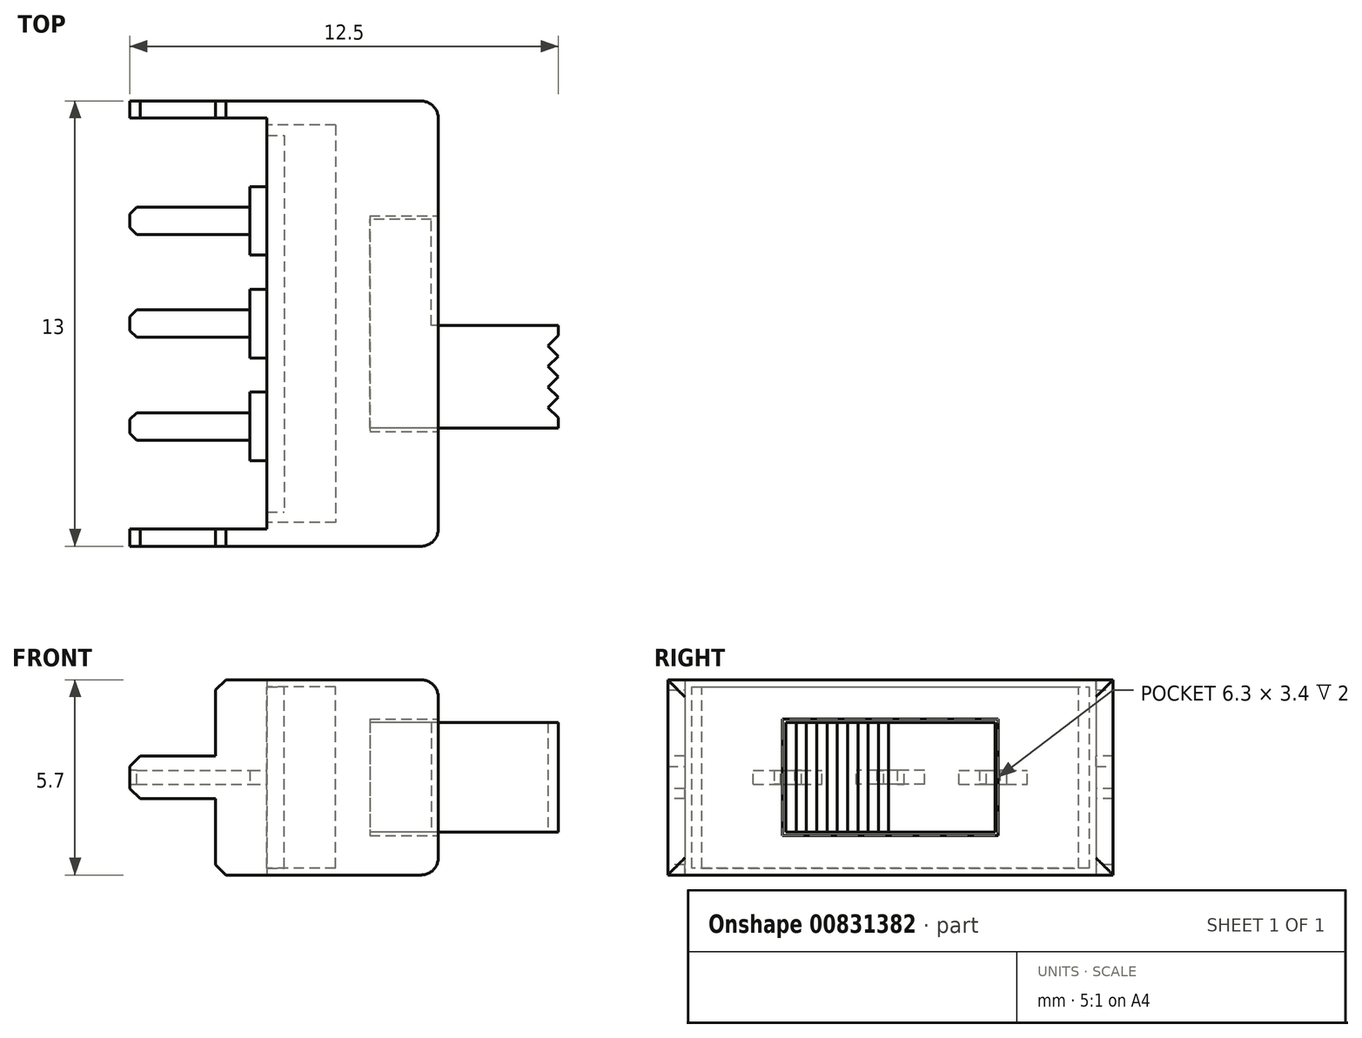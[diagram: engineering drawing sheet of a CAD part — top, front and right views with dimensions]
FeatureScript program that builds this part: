
annotation { "Feature Type Name" : "Feature", "Feature Type Description" : "" }
export const myFeature = defineFeature(function(context is Context, id is Id, definition is map)
    precondition{}
    {
        {
            var Q0;
            Q0=qCreatedBy(makeId("Top.planeOp"),FACE);
            var sketch = newSketch(context, id + "F0", { "sketchPlane" : qUnion([Q0])});
            skLineSegment(sketch, "E0.bottom", {"start": v(2.5, 6.5) * mm, "end": v(-2.5, 6.5) * mm});
            skLineSegment(sketch, "E0.top", {"start": v(2.5, -6.5) * mm, "end": v(-2.5, -6.5) * mm});
            skLineSegment(sketch, "E0.left", {"start": v(2.5, 6.5) * mm, "end": v(2.5, -6.5) * mm});
            skLineSegment(sketch, "E0.right", {"start": v(-2.5, 6.5) * mm, "end": v(-2.5, -6.5) * mm});
            skPoint(sketch, "E0.middle", {"position": v(0, 0) * mm});
            skSolve(sketch);
        }
        {
            var Q0;
            Q0=qSketchRegion(id+"F0",true);
            extrude(context, id + "F1", {"entities" : qUnion([Q0]), "depth" : 5.7 * mm, "offsetDistance" : 25 * mm});
        }
        {
            var Q0;
            Q0=makeQuery(id+"F1.opExtrude","SWEPT_FACE",FACE,{"disambiguationData":[OSD([sQuery(id+"F0.wireOp",EDGE,"E0.left")])]});
            var sketch = newSketch(context, id + "F2", { "sketchPlane" : qUnion([Q0])});
            skLineSegment(sketch, "E1.bottom", {"start": v(3.15, 4.55) * mm, "end": v(-3.15, 4.55) * mm});
            skLineSegment(sketch, "E1.top", {"start": v(3.15, 1.15) * mm, "end": v(-3.15, 1.15) * mm});
            skLineSegment(sketch, "E1.left", {"start": v(3.15, 4.55) * mm, "end": v(3.15, 1.15) * mm});
            skLineSegment(sketch, "E1.right", {"start": v(-3.15, 4.55) * mm, "end": v(-3.15, 1.15) * mm});
            skPoint(sketch, "E1.middle", {"position": v(0, 2.85) * mm});
            skPoint(sketch, "E1.middle.positionSnap0", {"position": v(-6.5, 2.85) * mm});
            skPoint(sketch, "E1.middle.positionSnap1", {"position": v(0, 5.7) * mm});
            skPoint(sketch, "E1.centerSnap0", {"position": v(-6.5, 2.85) * mm});
            skPoint(sketch, "E1.centerSnap1", {"position": v(0, 5.7) * mm});
            skSolve(sketch);
        }
        {
            var Q0;
            Q0=qSketchRegion(id+"F2",true);
            extrude(context, id + "F3", {"entities" : qUnion([Q0]), "operationType" : NewBodyOperationType.REMOVE, "oppositeDirection" : true, "depth" : 2 * mm, "offsetDistance" : 25 * mm});
        }
        {
            var Q0;
            Q0=makeQuery(id+"F3.boolean.opBoolean","COPY",FACE,{"derivedFrom":makeQuery(id+"F3.opExtrude","CAP_FACE",FACE,{"disambiguationData":[OSD([sQuery(id+"F2.wireOp",EDGE,"E1.bottom"),sQuery(id+"F2.wireOp",EDGE,"E1.top"),sQuery(id+"F2.wireOp",EDGE,"E1.left"),sQuery(id+"F2.wireOp",EDGE,"E1.right")])],"isStart":false})});
            var sketch = newSketch(context, id + "F4", { "sketchPlane" : qUnion([Q0])});
            skLineSegment(sketch, "E2.0", {"start": v(-3.05, 1.25) * mm, "end": v(3.05, 1.25) * mm});
            skLineSegment(sketch, "E2.1", {"start": v(-3.05, 4.45) * mm, "end": v(-3.05, 1.25) * mm});
            skLineSegment(sketch, "E2.2", {"start": v(3.05, 4.45) * mm, "end": v(-3.05, 4.45) * mm});
            skLineSegment(sketch, "E2.3", {"start": v(3.05, 1.25) * mm, "end": v(3.05, 4.45) * mm});
            skSolve(sketch);
        }
        {
            var Q0;
            Q0=makeQuery(id+"F4.imprint","IMPRINT",FACE,{"disambiguationData":[TD([[makeQuery(id+"F4.imprint","IMPRINT",EDGE,{"derivedFrom":sQuery(id+"F4.wireOp",EDGE,"E2.0")}),1.0]])]});
            extrude(context, id + "F5", {"entities" : qUnion([Q0]), "depth" : 1.8 * mm, "offsetDistance" : 25 * mm});
        }
        {
            var Q0;
            Q0=makeQuery(id+"F5.opExtrude","CAP_FACE",FACE,{"disambiguationData":[OSD([sQuery(id+"F4.wireOp",EDGE,"E2.0"),sQuery(id+"F4.wireOp",EDGE,"E2.1"),sQuery(id+"F4.wireOp",EDGE,"E2.2"),sQuery(id+"F4.wireOp",EDGE,"E2.3")])],"isStart":false});
            var sketch = newSketch(context, id + "F6", { "sketchPlane" : qUnion([Q0])});
            skLineSegment(sketch, "E3", {"start": v(-0.05, 4.45) * mm, "end": v(-0.05, 1.25) * mm});
            skSolve(sketch);
        }
        {
            var Q0;
            Q0=qSketchRegion(id+"F6",true);
            var Q1;
            {var subQ0=sQuery(id+"F6.wireOp",EDGE,"E3");Q1=makeQuery(id+"F6.imprint","IMPRINT",FACE,{"disambiguationData":[TD([[makeQuery(id+"F6.imprint","IMPRINT",EDGE,{"derivedFrom":subQ0}),-1.0]])]});}
            extrude(context, id + "F7", {"entities" : qUnion([Q0, Q1]), "operationType" : NewBodyOperationType.ADD, "depth" : 3.7 * mm, "offsetDistance" : 25 * mm});
        }
        {
            var Q0;
            Q0=makeQuery(id+"F1.opExtrude","SWEPT_FACE",FACE,{"disambiguationData":[OSD([sQuery(id+"F0.wireOp",EDGE,"E0.right")])]});
            var sketch = newSketch(context, id + "F8", { "sketchPlane" : qUnion([Q0])});
            skLineSegment(sketch, "E4", {"start": v(-6, 5.7) * mm, "end": v(-6, 0) * mm});
            skLineSegment(sketch, "E5", {"start": v(6, 5.7) * mm, "end": v(6, 0) * mm});
            skSolve(sketch);
        }
        {
            var Q0;
            Q0=qSketchRegion(id+"F8",true);
            var Q1;
            {var subQ0=sQuery(id+"F8.wireOp",EDGE,"E4");Q1=makeQuery(id+"F8.imprint","IMPRINT",FACE,{"disambiguationData":[TD([[makeQuery(id+"F8.imprint","IMPRINT",EDGE,{"derivedFrom":subQ0}),-1.0]])]});}
            var Q2;
            {var subQ0=sQuery(id+"F8.wireOp",EDGE,"E5");Q2=makeQuery(id+"F8.imprint","IMPRINT",FACE,{"disambiguationData":[TD([[makeQuery(id+"F8.imprint","IMPRINT",EDGE,{"derivedFrom":subQ0}),1.0]])]});}
            extrude(context, id + "F9", {"entities" : qUnion([Q0, Q1, Q2]), "operationType" : NewBodyOperationType.ADD, "depth" : 1.5 * mm, "offsetDistance" : 25 * mm});
        }
        {
            var Q0;
            Q0=makeQuery(id+"F1.opExtrude","CAP_EDGE",EDGE,{"disambiguationData":[OSD([sQuery(id+"F0.wireOp",EDGE,"E0.left")])],"isStart":false});
            var Q1;
            Q1=makeQuery(id+"F1.opExtrude","SWEPT_EDGE",EDGE,{"disambiguationData":[OSD([sQuery(id+"F0.wireOp",EDGE,"E0.bottom"),sQuery(id+"F0.wireOp",EDGE,"E0.left")])]});
            var Q2;
            Q2=makeQuery(id+"F1.opExtrude","CAP_EDGE",EDGE,{"disambiguationData":[OSD([sQuery(id+"F0.wireOp",EDGE,"E0.left")])],"isStart":true});
            var Q3;
            Q3=makeQuery(id+"F1.opExtrude","SWEPT_EDGE",EDGE,{"disambiguationData":[OSD([sQuery(id+"F0.wireOp",EDGE,"E0.top"),sQuery(id+"F0.wireOp",EDGE,"E0.left")])]});
            fillet(context, id + "F10", {"entities" : qUnion([Q0, Q1, Q2, Q3]), "radius" : 0.5 * mm, "tangentPropagation" : true, "allowEdgeOverflow" : false});
        }
        {
            var Q0;
            Q0=makeQuery(id+"F1.opExtrude","SWEPT_FACE",FACE,{"disambiguationData":[OSD([sQuery(id+"F0.wireOp",EDGE,"E0.right")])]});
            var sketch = newSketch(context, id + "F11", { "sketchPlane" : qUnion([Q0])});
            skLineSegment(sketch, "E6.0", {"start": v(5.8, 0.2) * mm, "end": v(5.8, 5.5) * mm});
            skLineSegment(sketch, "E6.1", {"start": v(-5.8, 0.2) * mm, "end": v(5.8, 0.2) * mm});
            skLineSegment(sketch, "E6.2", {"start": v(-5.8, 5.5) * mm, "end": v(-5.8, 0.2) * mm});
            skLineSegment(sketch, "E6.3", {"start": v(5.8, 5.5) * mm, "end": v(-5.8, 5.5) * mm});
            skSolve(sketch);
        }
        {
            var Q0;
            Q0=qSketchRegion(id+"F11",true);
            extrude(context, id + "F12", {"entities" : qUnion([Q0]), "operationType" : NewBodyOperationType.REMOVE, "oppositeDirection" : true, "depth" : 2 * mm, "offsetDistance" : 25 * mm});
        }
        {
            var Q0;
            Q0=makeQuery(id+"F12.boolean.opBoolean","COPY",FACE,{"derivedFrom":makeQuery(id+"F12.opExtrude","SWEPT_FACE",FACE,{"disambiguationData":[OSD([sQuery(id+"F11.wireOp",EDGE,"E6.3")])]})});
            var sketch = newSketch(context, id + "F13", { "sketchPlane" : qUnion([Q0])});
            skLineSegment(sketch, "E7.bottom", {"start": v(-2.5, -5.5) * mm, "end": v(-2, -5.5) * mm});
            skLineSegment(sketch, "E7.top", {"start": v(-2.5, 5.5) * mm, "end": v(-2, 5.5) * mm});
            skLineSegment(sketch, "E7.left", {"start": v(-2.5, -5.5) * mm, "end": v(-2.5, 5.5) * mm});
            skLineSegment(sketch, "E7.right", {"start": v(-2, -5.5) * mm, "end": v(-2, 5.5) * mm});
            skSolve(sketch);
        }
        {
            var Q0;
            Q0=qSketchRegion(id+"F13",true);
            extrude(context, id + "F14", {"entities" : qUnion([Q0]), "depth" : 5.3 * mm, "offsetDistance" : 25 * mm});
        }
        {
            var Q0;
            Q0=makeQuery(id+"F14.opExtrude","SWEPT_FACE",FACE,{"disambiguationData":[OSD([sQuery(id+"F13.wireOp",EDGE,"E7.left")])]});
            var sketch = newSketch(context, id + "F15", { "sketchPlane" : qUnion([Q0])});
            skLineSegment(sketch, "E8.bottom", {"start": v(-2, 2.65) * mm, "end": v(-4, 2.65) * mm});
            skLineSegment(sketch, "E8.top", {"start": v(-2, 3.05) * mm, "end": v(-4, 3.05) * mm});
            skLineSegment(sketch, "E8.left", {"start": v(-2, 2.65) * mm, "end": v(-2, 3.05) * mm});
            skLineSegment(sketch, "E8.right", {"start": v(-4, 2.65) * mm, "end": v(-4, 3.05) * mm});
            skPoint(sketch, "E8.middle", {"position": v(-3, 2.85) * mm});
            skPoint(sketch, "E8.middle.positionSnap0", {"position": v(-5.5, 2.85) * mm});
            skPoint(sketch, "E8.centerSnap0", {"position": v(-5.5, 2.85) * mm});
            skLineSegment(sketch, "E9.bottom", {"start": v(-1, 2.65) * mm, "end": v(1, 2.65) * mm});
            skLineSegment(sketch, "E9.top", {"start": v(-1, 3.05) * mm, "end": v(1, 3.05) * mm});
            skLineSegment(sketch, "E9.left", {"start": v(-1, 2.65) * mm, "end": v(-1, 3.05) * mm});
            skLineSegment(sketch, "E9.right", {"start": v(1, 2.65) * mm, "end": v(1, 3.05) * mm});
            skPoint(sketch, "E9.middle", {"position": v(0, 2.85) * mm});
            skPoint(sketch, "E9.middle.positionSnap0", {"position": v(-2, 2.85) * mm});
            skPoint(sketch, "E9.middle.positionSnap1", {"position": v(0, 5.5) * mm});
            skPoint(sketch, "E9.centerSnap0", {"position": v(-2, 2.85) * mm});
            skPoint(sketch, "E9.centerSnap1", {"position": v(0, 5.5) * mm});
            skLineSegment(sketch, "E10.bottom", {"start": v(4, 2.65) * mm, "end": v(2, 2.65) * mm});
            skLineSegment(sketch, "E10.top", {"start": v(4, 3.05) * mm, "end": v(2, 3.05) * mm});
            skLineSegment(sketch, "E10.left", {"start": v(4, 2.65) * mm, "end": v(4, 3.05) * mm});
            skLineSegment(sketch, "E10.right", {"start": v(2, 2.65) * mm, "end": v(2, 3.05) * mm});
            skPoint(sketch, "E10.middle", {"position": v(3, 2.85) * mm});
            skSolve(sketch);
        }
        {
            var Q0;
            {var subQ0=sQuery(id+"F4.wireOp",EDGE,"E2.0");Q0=makeQuery(id+"F7.boolean.opBoolean","MERGE",FACE,{"derivedFrom":[makeQuery(id+"F5.opExtrude","SWEPT_FACE",FACE,{"disambiguationData":[OSD([subQ0])]}),makeQuery(id+"F7.opExtrude","SWEPT_FACE",FACE,{"disambiguationData":[OSD([subQ0])]})]});}
            var sketch = newSketch(context, id + "F16", { "sketchPlane" : qUnion([Q0])});
            skLineSegment(sketch, "E11", {"start": v(6, 3.05) * mm, "end": v(6, 2.75) * mm});
            skLineSegment(sketch, "E12", {"start": v(6, 2.75) * mm, "end": v(5.7, 2.45) * mm});
            skLineSegment(sketch, "E13", {"start": v(5.7, 2.45) * mm, "end": v(6, 2.15) * mm});
            skLineSegment(sketch, "E14", {"start": v(6, 2.15) * mm, "end": v(5.7, 1.85) * mm});
            skLineSegment(sketch, "E15", {"start": v(5.7, 1.85) * mm, "end": v(6, 1.55) * mm});
            skLineSegment(sketch, "E16", {"start": v(6, 1.55) * mm, "end": v(5.7, 1.25) * mm});
            skLineSegment(sketch, "E17", {"start": v(5.7, 1.25) * mm, "end": v(6, 0.95) * mm});
            skLineSegment(sketch, "E18", {"start": v(6, 0.95) * mm, "end": v(5.7, 0.65) * mm});
            skLineSegment(sketch, "E19", {"start": v(5.7, 0.65) * mm, "end": v(6, 0.35) * mm});
            skLineSegment(sketch, "E20", {"start": v(6, 0.35) * mm, "end": v(6, 0.05) * mm});
            skSolve(sketch);
        }
        {
            var Q0;
            {var subQ0=sQuery(id+"F16.wireOp",EDGE,"E12");Q0=makeQuery(id+"F16.imprint","IMPRINT",FACE,{"disambiguationData":[TD([[makeQuery(id+"F16.imprint","IMPRINT",EDGE,{"derivedFrom":subQ0}),1.0]])]});}
            var Q1;
            {var subQ0=sQuery(id+"F16.wireOp",EDGE,"E14");Q1=makeQuery(id+"F16.imprint","IMPRINT",FACE,{"disambiguationData":[TD([[makeQuery(id+"F16.imprint","IMPRINT",EDGE,{"derivedFrom":subQ0}),1.0]])]});}
            var Q2;
            {var subQ0=sQuery(id+"F16.wireOp",EDGE,"E16");Q2=makeQuery(id+"F16.imprint","IMPRINT",FACE,{"disambiguationData":[TD([[makeQuery(id+"F16.imprint","IMPRINT",EDGE,{"derivedFrom":subQ0}),1.0]])]});}
            var Q3;
            {var subQ0=sQuery(id+"F16.wireOp",EDGE,"E18");Q3=makeQuery(id+"F16.imprint","IMPRINT",FACE,{"disambiguationData":[TD([[makeQuery(id+"F16.imprint","IMPRINT",EDGE,{"derivedFrom":subQ0}),1.0]])]});}
            extrude(context, id + "F17", {"entities" : qUnion([Q0, Q1, Q2, Q3]), "operationType" : NewBodyOperationType.REMOVE, "oppositeDirection" : true, "depth" : 25 * mm, "offsetDistance" : 25 * mm});
        }
        {
            var Q0;
            Q0=makeQuery(id+"F15.imprint","IMPRINT",FACE,{"disambiguationData":[TD([[makeQuery(id+"F15.imprint","IMPRINT",EDGE,{"derivedFrom":sQuery(id+"F15.wireOp",EDGE,"E8.bottom")}),-1.0]])]});
            var Q1;
            Q1=makeQuery(id+"F15.imprint","IMPRINT",FACE,{"disambiguationData":[TD([[makeQuery(id+"F15.imprint","IMPRINT",EDGE,{"derivedFrom":sQuery(id+"F15.wireOp",EDGE,"E9.bottom")}),1.0]])]});
            var Q2;
            Q2=makeQuery(id+"F15.imprint","IMPRINT",FACE,{"disambiguationData":[TD([[makeQuery(id+"F15.imprint","IMPRINT",EDGE,{"derivedFrom":sQuery(id+"F15.wireOp",EDGE,"E10.bottom")}),-1.0]])]});
            extrude(context, id + "F18", {"entities" : qUnion([Q0, Q1, Q2]), "depth" : 0.5 * mm, "offsetDistance" : 25 * mm});
        }
        {
            var Q0;
            Q0=makeQuery(id+"F18.opExtrude","CAP_FACE",FACE,{"disambiguationData":[OSD([sQuery(id+"F15.wireOp",EDGE,"E8.bottom"),sQuery(id+"F15.wireOp",EDGE,"E8.top"),sQuery(id+"F15.wireOp",EDGE,"E8.left"),sQuery(id+"F15.wireOp",EDGE,"E8.right")])],"isStart":false});
            var sketch = newSketch(context, id + "F19", { "sketchPlane" : qUnion([Q0])});
            skLineSegment(sketch, "E21", {"start": v(-3.4, 3.05) * mm, "end": v(-3.4, 2.65) * mm});
            skLineSegment(sketch, "E22", {"start": v(-2.6, 3.05) * mm, "end": v(-2.6, 2.65) * mm});
            skSolve(sketch);
        }
        {
            var Q0;
            Q0=makeQuery(id+"F18.opExtrude","CAP_FACE",FACE,{"disambiguationData":[OSD([sQuery(id+"F15.wireOp",EDGE,"E9.bottom"),sQuery(id+"F15.wireOp",EDGE,"E9.top"),sQuery(id+"F15.wireOp",EDGE,"E9.left"),sQuery(id+"F15.wireOp",EDGE,"E9.right")])],"isStart":false});
            var sketch = newSketch(context, id + "F20", { "sketchPlane" : qUnion([Q0])});
            skLineSegment(sketch, "E23", {"start": v(-0.4, 3.05) * mm, "end": v(-0.4, 2.65) * mm});
            skLineSegment(sketch, "E24", {"start": v(0.4, 3.05) * mm, "end": v(0.4, 2.65) * mm});
            skSolve(sketch);
        }
        {
            var Q0;
            Q0=makeQuery(id+"F18.opExtrude","CAP_FACE",FACE,{"disambiguationData":[OSD([sQuery(id+"F15.wireOp",EDGE,"E10.bottom"),sQuery(id+"F15.wireOp",EDGE,"E10.top"),sQuery(id+"F15.wireOp",EDGE,"E10.left"),sQuery(id+"F15.wireOp",EDGE,"E10.right")])],"isStart":false});
            var sketch = newSketch(context, id + "F21", { "sketchPlane" : qUnion([Q0])});
            skLineSegment(sketch, "E25", {"start": v(2.6, 3.05) * mm, "end": v(2.6, 2.65) * mm});
            skLineSegment(sketch, "E26", {"start": v(3.4, 3.05) * mm, "end": v(3.4, 2.65) * mm});
            skSolve(sketch);
        }
        {
            var Q0;
            {var subQ0=sQuery(id+"F19.wireOp",EDGE,"E21");Q0=makeQuery(id+"F19.imprint","IMPRINT",FACE,{"disambiguationData":[TD([[makeQuery(id+"F19.imprint","IMPRINT",EDGE,{"derivedFrom":subQ0}),1.0]])]});}
            var Q1;
            {var subQ0=sQuery(id+"F20.wireOp",EDGE,"E23");Q1=makeQuery(id+"F20.imprint","IMPRINT",FACE,{"disambiguationData":[TD([[makeQuery(id+"F20.imprint","IMPRINT",EDGE,{"derivedFrom":subQ0}),1.0]])]});}
            var Q2;
            {var subQ0=sQuery(id+"F21.wireOp",EDGE,"E25");Q2=makeQuery(id+"F21.imprint","IMPRINT",FACE,{"disambiguationData":[TD([[makeQuery(id+"F21.imprint","IMPRINT",EDGE,{"derivedFrom":subQ0}),1.0]])]});}
            extrude(context, id + "F22", {"entities" : qUnion([Q0, Q1, Q2]), "depth" : 3.5 * mm, "offsetDistance" : 25 * mm});
        }
        {
            var Q0;
            Q0=makeQuery(id+"F9.opExtrude","CAP_FACE",FACE,{"disambiguationData":[OSD([sQuery(id+"F0.wireOp",EDGE,"E0.bottom"),sQuery(id+"F0.wireOp",EDGE,"E0.right"),sQuery(id+"F8.wireOp",EDGE,"E4")])],"isStart":false});
            var sketch = newSketch(context, id + "F23", { "sketchPlane" : qUnion([Q0])});
            skLineSegment(sketch, "E27", {"start": v(-6.5, 3.48) * mm, "end": v(-6, 3.48) * mm});
            skLineSegment(sketch, "E28", {"start": v(-6.5, 2.23) * mm, "end": v(-6, 2.23) * mm});
            skLineSegment(sketch, "E29", {"start": v(-6.5, 2.85) * mm, "end": v(-6, 2.85) * mm, "construction": true});
            skSolve(sketch);
        }
        {
            var Q0;
            Q0=makeQuery(id+"F9.opExtrude","CAP_FACE",FACE,{"disambiguationData":[OSD([sQuery(id+"F0.wireOp",EDGE,"E0.top"),sQuery(id+"F0.wireOp",EDGE,"E0.right"),sQuery(id+"F8.wireOp",EDGE,"E5")])],"isStart":false});
            var sketch = newSketch(context, id + "F24", { "sketchPlane" : qUnion([Q0])});
            skLineSegment(sketch, "E30", {"start": v(6, 3.48) * mm, "end": v(6.5, 3.48) * mm});
            skLineSegment(sketch, "E31", {"start": v(6, 2.23) * mm, "end": v(6.5, 2.23) * mm});
            skLineSegment(sketch, "E32", {"start": v(6, 2.85) * mm, "end": v(6.5, 2.85) * mm, "construction": true});
            skSolve(sketch);
        }
        {
            var Q0;
            {var subQ0=sQuery(id+"F23.wireOp",EDGE,"E27");Q0=makeQuery(id+"F23.imprint","IMPRINT",FACE,{"disambiguationData":[TD([[makeQuery(id+"F23.imprint","IMPRINT",EDGE,{"derivedFrom":subQ0}),-1.0]])]});}
            var Q1;
            {var subQ0=sQuery(id+"F24.wireOp",EDGE,"E30");Q1=makeQuery(id+"F24.imprint","IMPRINT",FACE,{"disambiguationData":[TD([[makeQuery(id+"F24.imprint","IMPRINT",EDGE,{"derivedFrom":subQ0}),-1.0]])]});}
            extrude(context, id + "F25", {"entities" : qUnion([Q0, Q1]), "operationType" : NewBodyOperationType.ADD, "depth" : 2.5 * mm, "offsetDistance" : 25 * mm});
        }
        {
            var Q0;
            Q0=makeQuery(id+"F22.opExtrude","CAP_EDGE",EDGE,{"disambiguationData":[OSD([sQuery(id+"F19.wireOp",EDGE,"E21")])],"isStart":false});
            var Q1;
            Q1=makeQuery(id+"F22.opExtrude","CAP_EDGE",EDGE,{"disambiguationData":[OSD([sQuery(id+"F19.wireOp",EDGE,"E22")])],"isStart":false});
            var Q2;
            Q2=makeQuery(id+"F22.opExtrude","CAP_EDGE",EDGE,{"disambiguationData":[OSD([sQuery(id+"F20.wireOp",EDGE,"E23")])],"isStart":false});
            var Q3;
            Q3=makeQuery(id+"F22.opExtrude","CAP_EDGE",EDGE,{"disambiguationData":[OSD([sQuery(id+"F20.wireOp",EDGE,"E24")])],"isStart":false});
            var Q4;
            Q4=makeQuery(id+"F22.opExtrude","CAP_EDGE",EDGE,{"disambiguationData":[OSD([sQuery(id+"F21.wireOp",EDGE,"E25")])],"isStart":false});
            var Q5;
            Q5=makeQuery(id+"F22.opExtrude","CAP_EDGE",EDGE,{"disambiguationData":[OSD([sQuery(id+"F21.wireOp",EDGE,"E26")])],"isStart":false});
            chamfer(context, id + "F26", {"entities" : qUnion([Q0, Q1, Q2, Q3, Q4, Q5]), "width" : 0.2 * mm, "tangentPropagation" : true});
        }
        {
            var Q0;
            Q0=makeQuery(id+"F25.opExtrude","CAP_EDGE",EDGE,{"disambiguationData":[OSD([sQuery(id+"F24.wireOp",EDGE,"E30")])],"isStart":false});
            var Q1;
            Q1=makeQuery(id+"F25.opExtrude","CAP_EDGE",EDGE,{"disambiguationData":[OSD([sQuery(id+"F24.wireOp",EDGE,"E31")])],"isStart":false});
            var Q2;
            Q2=makeQuery(id+"F25.opExtrude","CAP_EDGE",EDGE,{"disambiguationData":[OSD([sQuery(id+"F23.wireOp",EDGE,"E27")])],"isStart":false});
            var Q3;
            Q3=makeQuery(id+"F25.opExtrude","CAP_EDGE",EDGE,{"disambiguationData":[OSD([sQuery(id+"F23.wireOp",EDGE,"E28")])],"isStart":false});
            chamfer(context, id + "F27", {"entities" : qUnion([Q0, Q1, Q2, Q3]), "width" : 0.3 * mm, "tangentPropagation" : true});
        }
        {
            var Q0;
            {var subQ0=sQuery(id+"F0.wireOp",EDGE,"E0.right");var subQ1=makeQuery(id+"F1.opExtrude","CAP_EDGE",EDGE,{"disambiguationData":[OSD([subQ0])],"isStart":false});Q0=makeQuery(id+"F9.opExtrude","CAP_EDGE",EDGE,{"disambiguationData":[OSD([subQ0]),TDD([makeQuery(id+"F8.imprint","IMPRINT",EDGE,{"disambiguationData":[TD([[makeQuery(id+"F8.imprint","INTERSECT",VERTEX,{"derivedFrom":[subQ1,sQuery(id+"F8.wireOp",EDGE,"E4")]}),1.0]])],"derivedFrom":subQ1})])],"isStart":false});}
            var Q1;
            {var subQ0=sQuery(id+"F0.wireOp",EDGE,"E0.right");var subQ1=makeQuery(id+"F1.opExtrude","CAP_EDGE",EDGE,{"disambiguationData":[OSD([subQ0])],"isStart":true});Q1=makeQuery(id+"F9.opExtrude","CAP_EDGE",EDGE,{"disambiguationData":[OSD([subQ0]),TDD([makeQuery(id+"F8.imprint","IMPRINT",EDGE,{"disambiguationData":[TD([[makeQuery(id+"F8.imprint","INTERSECT",VERTEX,{"derivedFrom":[subQ1,sQuery(id+"F8.wireOp",EDGE,"E4")]}),1.0]])],"derivedFrom":subQ1})])],"isStart":false});}
            var Q2;
            {var subQ0=sQuery(id+"F0.wireOp",EDGE,"E0.right");var subQ1=makeQuery(id+"F1.opExtrude","CAP_EDGE",EDGE,{"disambiguationData":[OSD([subQ0])],"isStart":false});Q2=makeQuery(id+"F9.opExtrude","CAP_EDGE",EDGE,{"disambiguationData":[OSD([subQ0]),TDD([makeQuery(id+"F8.imprint","IMPRINT",EDGE,{"disambiguationData":[TD([[makeQuery(id+"F8.imprint","INTERSECT",VERTEX,{"derivedFrom":[subQ1,sQuery(id+"F8.wireOp",EDGE,"E5")]}),-1.0]])],"derivedFrom":subQ1})])],"isStart":false});}
            var Q3;
            {var subQ0=sQuery(id+"F0.wireOp",EDGE,"E0.right");var subQ1=makeQuery(id+"F1.opExtrude","CAP_EDGE",EDGE,{"disambiguationData":[OSD([subQ0])],"isStart":true});Q3=makeQuery(id+"F9.opExtrude","CAP_EDGE",EDGE,{"disambiguationData":[OSD([subQ0]),TDD([makeQuery(id+"F8.imprint","IMPRINT",EDGE,{"disambiguationData":[TD([[makeQuery(id+"F8.imprint","INTERSECT",VERTEX,{"derivedFrom":[subQ1,sQuery(id+"F8.wireOp",EDGE,"E5")]}),-1.0]])],"derivedFrom":subQ1})])],"isStart":false});}
            chamfer(context, id + "F28", {"entities" : qUnion([Q0, Q1, Q2, Q3]), "width" : 0.3 * mm, "tangentPropagation" : true});
        }
    });
